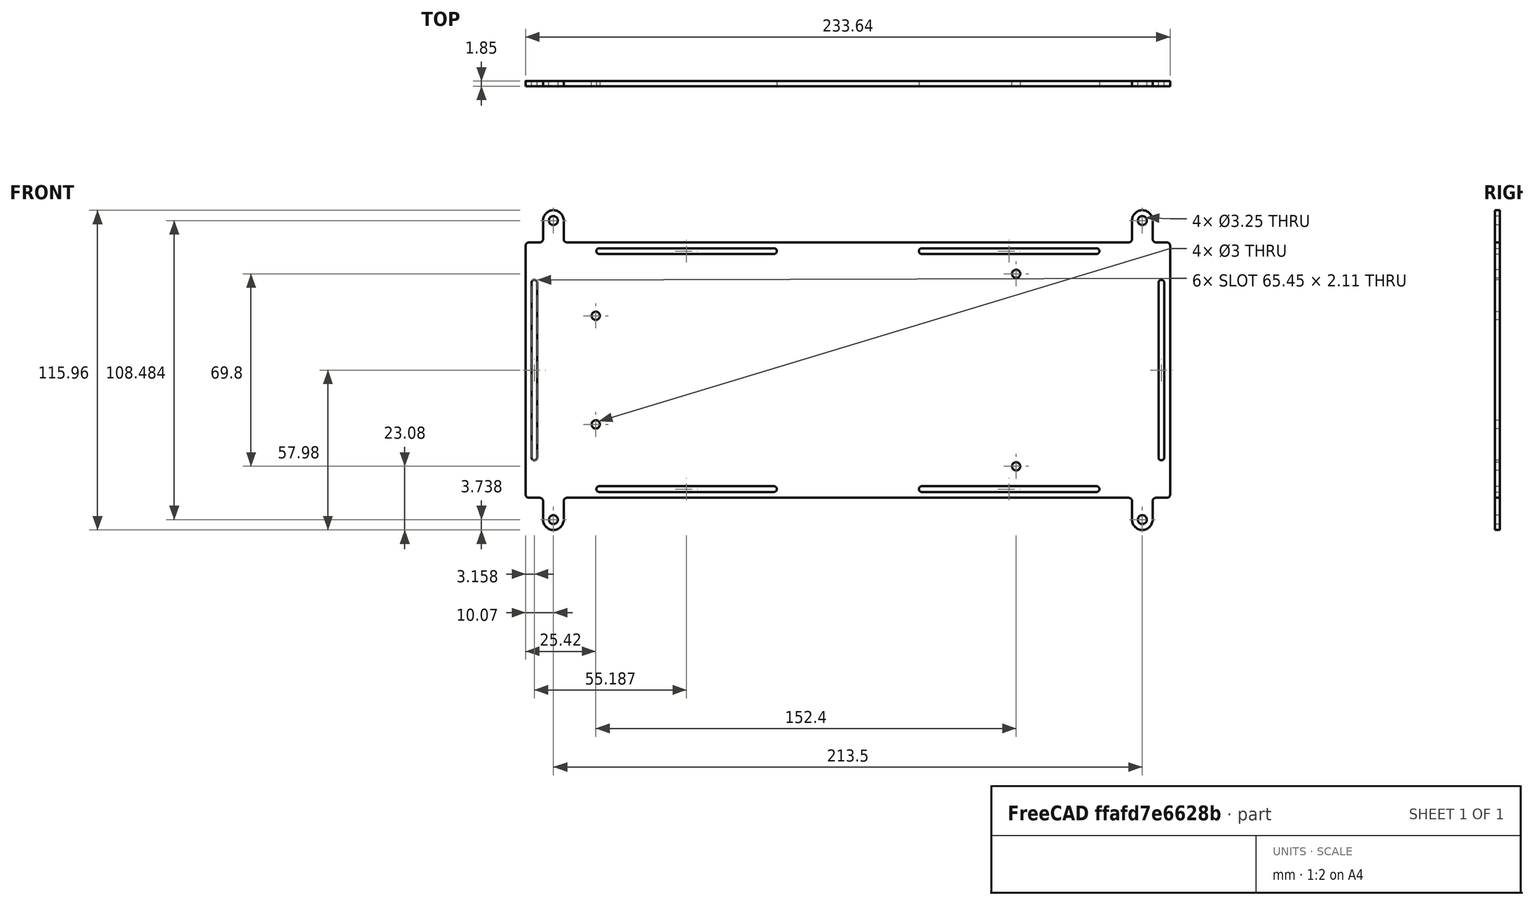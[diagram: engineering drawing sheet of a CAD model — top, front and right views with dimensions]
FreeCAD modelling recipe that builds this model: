
FCSTD DOCUMENT  (FreeCAD 1.0R38641 +468 (Git))
Label: psu_top_and_bottom
License: All rights reserved
LicenseURL: https://en.wikipedia.org/wiki/All_rights_reserved
objects: PartDesign::SubShapeBinder×2, Sketcher::SketchObject×1, PartDesign::Pad×1, PartDesign::Body×1
note: 8 computed .brp shape members not serialized (recipe doc carries the construction recipe); baked Part::Feature solids carry a one-line shape summary decoded from their .brp
EXTERNAL_REF file=../panel_back.FCStd obj=Body
EXTERNAL_REF file=../../third_party/doepfer_psu3.FCStd obj=Sketch
EXTERNAL_REF file=../panel_back.FCStd obj=Sketch
EXTERNAL_REF file=../../third_party/doepfer_psu3.FCStd obj=Body
EXTERNAL_REF file=../dimensions.FCStd obj=VarSet

FEATURE [PartDesign::SubShapeBinder] Binder  label="PanelBackBinder"
  BindCopyOnChange = 0
  BindMode = 0
  ClaimChildren = false
  Context = -> Body [Binder.]
  Fuse = false
  MakeFace = true
  OffsetFill = false
  OffsetIntersection = false
  OffsetJoinType = 0
  OffsetOpenResult = false
  PartialLoad = false
  Refine = true
  Relative = true
  Support = -> [<external ../panel_back.FCStd>#Body]
  _Version = 2
FEATURE [PartDesign::SubShapeBinder] Binder001  label="Psu3Binder"
  BindCopyOnChange = 0
  BindMode = 0
  ClaimChildren = false
  Context = -> Body [Binder001.]
  Fuse = false
  MakeFace = true
  OffsetFill = false
  OffsetIntersection = false
  OffsetJoinType = 0
  OffsetOpenResult = false
  PartialLoad = false
  Placement = pos=(103,130,-16.25) rot=(1,0,0;-1.5708rad)
  Refine = true
  Relative = true
  Support = -> [<external ../../third_party/doepfer_psu3.FCStd>#Body]
  _Version = 2
  expr: .Placement.Base.x = (panel_back#Sketch.Constraints.DeltaX - panel_back#Sketch.Constraints.OffsetX - doepfer_psu3#Sketch.Constraints.Width) / 2 - 10 mm
  expr: .Placement.Base.z = (doepfer_psu3#Sketch.Constraints.Height - (panel_back#Sketch.Constraints.DeltaY - panel_back#Sketch.Constraints.OffsetY)) / 2
FEATURE [Sketcher::SketchObject] Sketch
  ArcFitTolerance = 1e-06
  AttachmentSupport = -> [Binder]
  ExternalGeometry = -> [Binder001,Binder]
  FullyConstrained = true
  MakeInternals = false
  MapMode = 5
  Placement = pos=(0,127.227,-5.85e-14) rot=(0,0.707107,0.707107;3.14159rad)
  expr: Constraints[113] = dimensions#VarSet.EnclosureFinishThickness
  expr: Constraints[36] = dimensions#VarSet.EnclosureTotalThickness + 2 * dimensions#VarSet.EnclosureFinishThickness
  sketch-geometry (95):
    g0: LineSegment StartX=-330.325 StartY=-11.1254 StartZ=0 EndX=-330.325 EndY=-101.375 EndZ=0
    g1: LineSegment StartX=-96.6754 StartY=-101.375 StartZ=0 EndX=-96.6754 EndY=-11.1254 EndZ=0
    g2: Circle CenterX=-320.25 CenterY=-2.0081 CenterZ=0 NormalX=0 NormalY=0 NormalZ=1 AngleXU=0 Radius=1.627
    g3: Circle CenterX=-106.75 CenterY=-2.0081 CenterZ=0 NormalX=0 NormalY=0 NormalZ=1 AngleXU=0 Radius=1.627
    g4: Circle CenterX=-122.1 CenterY=-36.55 CenterZ=0 NormalX=0 NormalY=0 NormalZ=1 AngleXU=0 Radius=1.5
    g5: Circle CenterX=-122.1 CenterY=-75.95 CenterZ=0 NormalX=0 NormalY=0 NormalZ=1 AngleXU=0 Radius=1.5
    g6: Circle CenterX=-106.75 CenterY=-110.492 CenterZ=0 NormalX=0 NormalY=0 NormalZ=1 AngleXU=0 Radius=1.627
    g7: Circle CenterX=-320.25 CenterY=-110.492 CenterZ=0 NormalX=0 NormalY=0 NormalZ=1 AngleXU=0 Radius=1.627
    g8: Circle CenterX=-274.5 CenterY=-91.15 CenterZ=0 NormalX=0 NormalY=0 NormalZ=1 AngleXU=0 Radius=1.5
    g9: Circle CenterX=-274.5 CenterY=-21.35 CenterZ=0 NormalX=0 NormalY=0 NormalZ=1 AngleXU=0 Radius=1.5
    g10: ArcOfCircle CenterX=-329.125 CenterY=-11.1254 CenterZ=0 NormalX=0 NormalY=0 NormalZ=1 AngleXU=0 Radius=1.2 StartAngle=1.5708 EndAngle=3.14159
    g11: GeomPoint [constr] X=-330.325 Y=-9.9254 Z=0
    g12: ArcOfCircle CenterX=-329.125 CenterY=-101.375 CenterZ=0 NormalX=0 NormalY=0 NormalZ=1 AngleXU=0 Radius=1.2 StartAngle=3.14159 EndAngle=4.71239
    g13: GeomPoint [constr] X=-330.325 Y=-102.575 Z=0
    g14: ArcOfCircle CenterX=-97.8754 CenterY=-101.375 CenterZ=0 NormalX=0 NormalY=0 NormalZ=1 AngleXU=0 Radius=1.2 StartAngle=4.71239 EndAngle=6.28319
    g15: GeomPoint [constr] X=-96.6754 Y=-102.575 Z=0
    g16: ArcOfCircle CenterX=-97.8754 CenterY=-11.1254 CenterZ=0 NormalX=0 NormalY=0 NormalZ=1 AngleXU=0 Radius=1.2 StartAngle=2e-16 EndAngle=1.5708
    g17: GeomPoint [constr] X=-96.6754 Y=-9.9254 Z=0
    g18: ArcOfCircle CenterX=-327.162 CenterY=-24.579 CenterZ=0 NormalX=0 NormalY=0 NormalZ=1 AngleXU=0 Radius=1.0541 StartAngle=-9e-16 EndAngle=3.14159
    g19: ArcOfCircle CenterX=-327.162 CenterY=-87.921 CenterZ=0 NormalX=0 NormalY=0 NormalZ=1 AngleXU=0 Radius=1.0541 StartAngle=3.14159 EndAngle=6.28319
    g20: LineSegment StartX=-326.108 StartY=-24.579 StartZ=0 EndX=-326.108 EndY=-87.921 EndZ=0
    g21: LineSegment StartX=-328.216 StartY=-24.579 StartZ=0 EndX=-328.216 EndY=-87.921 EndZ=0
    g22: LineSegment [constr] StartX=-330.325 StartY=-56.25 StartZ=0 EndX=-328.216 EndY=-56.25 EndZ=0
    g23: ArcOfCircle CenterX=-99.8377 CenterY=-24.579 CenterZ=0 NormalX=0 NormalY=0 NormalZ=1 AngleXU=0 Radius=1.0541 StartAngle=-9e-16 EndAngle=3.14159
    g24: ArcOfCircle CenterX=-99.8377 CenterY=-87.921 CenterZ=0 NormalX=0 NormalY=0 NormalZ=1 AngleXU=0 Radius=1.0541 StartAngle=3.14159 EndAngle=6.28319
    g25: LineSegment StartX=-98.7836 StartY=-24.579 StartZ=0 EndX=-98.7836 EndY=-87.921 EndZ=0
    g26: LineSegment StartX=-100.892 StartY=-24.579 StartZ=0 EndX=-100.892 EndY=-87.921 EndZ=0
    g27: LineSegment [constr] StartX=-98.7836 StartY=-56.25 StartZ=0 EndX=-96.6754 EndY=-56.25 EndZ=0
    g28: ArcOfCircle CenterX=-303.647 CenterY=-13.0877 CenterZ=0 NormalX=0 NormalY=0 NormalZ=1 AngleXU=0 Radius=1.0541 StartAngle=1.5708 EndAngle=4.71239
    g29: ArcOfCircle CenterX=-240.305 CenterY=-13.0877 CenterZ=0 NormalX=0 NormalY=0 NormalZ=1 AngleXU=0 Radius=1.0541 StartAngle=4.71239 EndAngle=7.85398
    g30: LineSegment StartX=-303.647 StartY=-12.0336 StartZ=0 EndX=-240.305 EndY=-12.0336 EndZ=0
    g31: LineSegment StartX=-303.647 StartY=-14.1418 StartZ=0 EndX=-240.305 EndY=-14.1418 EndZ=0
    g32: ArcOfCircle CenterX=-186.695 CenterY=-13.0877 CenterZ=0 NormalX=0 NormalY=0 NormalZ=1 AngleXU=0 Radius=1.0541 StartAngle=1.5708 EndAngle=4.71239
    g33: ArcOfCircle CenterX=-123.353 CenterY=-13.0877 CenterZ=0 NormalX=0 NormalY=0 NormalZ=1 AngleXU=0 Radius=1.0541 StartAngle=4.71239 EndAngle=7.85398
    g34: LineSegment StartX=-186.695 StartY=-12.0336 StartZ=0 EndX=-123.353 EndY=-12.0336 EndZ=0
    g35: LineSegment StartX=-186.695 StartY=-14.1418 StartZ=0 EndX=-123.353 EndY=-14.1418 EndZ=0
    g36: ArcOfCircle CenterX=-303.647 CenterY=-99.4123 CenterZ=0 NormalX=0 NormalY=0 NormalZ=1 AngleXU=0 Radius=1.0541 StartAngle=1.5708 EndAngle=4.71239
    g37: ArcOfCircle CenterX=-240.305 CenterY=-99.4123 CenterZ=0 NormalX=0 NormalY=0 NormalZ=1 AngleXU=0 Radius=1.0541 StartAngle=4.71239 EndAngle=7.85398
    g38: LineSegment StartX=-303.647 StartY=-98.3582 StartZ=0 EndX=-240.305 EndY=-98.3582 EndZ=0
    g39: LineSegment StartX=-303.647 StartY=-100.466 StartZ=0 EndX=-240.305 EndY=-100.466 EndZ=0
    g40: ArcOfCircle CenterX=-186.695 CenterY=-99.4123 CenterZ=0 NormalX=0 NormalY=0 NormalZ=1 AngleXU=0 Radius=1.0541 StartAngle=1.5708 EndAngle=4.71239
    g41: ArcOfCircle CenterX=-123.353 CenterY=-99.4123 CenterZ=0 NormalX=0 NormalY=0 NormalZ=1 AngleXU=0 Radius=1.0541 StartAngle=4.71239 EndAngle=7.85398
    g42: LineSegment StartX=-186.695 StartY=-98.3582 StartZ=0 EndX=-123.353 EndY=-98.3582 EndZ=0
    g43: LineSegment StartX=-186.695 StartY=-100.466 StartZ=0 EndX=-123.353 EndY=-100.466 EndZ=0
    g44: LineSegment [constr] StartX=-271.976 StartY=-100.466 StartZ=0 EndX=-271.976 EndY=-102.575 EndZ=0
    g45: LineSegment [constr] StartX=-155.024 StartY=-100.466 StartZ=0 EndX=-155.024 EndY=-102.575 EndZ=0
    g46: LineSegment [constr] StartX=-155.024 StartY=-12.0336 StartZ=0 EndX=-155.024 EndY=-9.9254 EndZ=0
    g47: LineSegment [constr] StartX=-271.976 StartY=-12.0336 StartZ=0 EndX=-271.976 EndY=-9.9254 EndZ=0
    g48: LineSegment [constr] StartX=-271.976 StartY=-98.3582 StartZ=0 EndX=-271.976 EndY=-14.1418 EndZ=0
    g49: LineSegment [constr] StartX=-155.024 StartY=-14.1418 StartZ=0 EndX=-155.024 EndY=-98.3582 EndZ=0
    g50: LineSegment [constr] StartX=-257.002 StartY=2.8729 StartZ=0 EndX=-257.002 EndY=-9.9254 EndZ=0
    g51: LineSegment [constr] StartX=-257.002 StartY=-115.373 StartZ=0 EndX=-257.002 EndY=-102.575 EndZ=0
    g52: LineSegment [constr] StartX=-328.216 StartY=-56.25 StartZ=0 EndX=-326.108 EndY=-56.25 EndZ=0
    g53: LineSegment [constr] StartX=-213.5 StartY=-9.9254 StartZ=0 EndX=-213.5 EndY=-102.575 EndZ=0
    g54: LineSegment [constr] StartX=-213.627 StartY=-9.9254 StartZ=0 EndX=-213.627 EndY=-102.575 EndZ=0
    g55: LineSegment [constr] StartX=-330.325 StartY=-98.3582 StartZ=0 EndX=-271.976 EndY=-98.3582 EndZ=0
    g56: LineSegment [constr] StartX=-271.976 StartY=-98.3582 StartZ=0 EndX=-213.627 EndY=-98.3582 EndZ=0
    g57: LineSegment [constr] StartX=-155.024 StartY=-98.3582 StartZ=0 EndX=-96.6754 EndY=-98.3582 EndZ=0
    g58: LineSegment [constr] StartX=-240.305 StartY=-14.1418 StartZ=0 EndX=-240.305 EndY=-16.25 EndZ=0
    g59: LineSegment [constr] StartX=-103 StartY=-56.25 StartZ=0 EndX=-100.892 EndY=-56.25 EndZ=0
    g60: ArcOfCircle CenterX=-320.25 CenterY=-2.0081 CenterZ=0 NormalX=0 NormalY=0 NormalZ=1 AngleXU=0 Radius=3.7352 StartAngle=0 EndAngle=3.14159
    g61: LineSegment StartX=-316.515 StartY=-2.0081 StartZ=0 EndX=-316.515 EndY=-8.7254 EndZ=0
    g62: LineSegment StartX=-325.185 StartY=-9.9254 StartZ=0 EndX=-329.125 EndY=-9.9254 EndZ=0
    g63: LineSegment StartX=-329.125 StartY=-102.575 StartZ=0 EndX=-325.185 EndY=-102.575 EndZ=0
    g64: LineSegment StartX=-315.315 StartY=-102.575 StartZ=0 EndX=-111.685 EndY=-102.575 EndZ=0
    g65: LineSegment StartX=-101.815 StartY=-102.575 StartZ=0 EndX=-97.8754 EndY=-102.575 EndZ=0
    g66: LineSegment StartX=-111.685 StartY=-9.9254 StartZ=0 EndX=-315.315 EndY=-9.9254 EndZ=0
    g67: LineSegment StartX=-97.8754 StartY=-9.9254 StartZ=0 EndX=-101.815 EndY=-9.9254 EndZ=0
    g68: ArcOfCircle CenterX=-320.25 CenterY=-110.492 CenterZ=0 NormalX=0 NormalY=0 NormalZ=1 AngleXU=0 Radius=3.7352 StartAngle=3.14159 EndAngle=6.28319
    g69: ArcOfCircle CenterX=-106.75 CenterY=-110.492 CenterZ=0 NormalX=0 NormalY=0 NormalZ=1 AngleXU=0 Radius=3.7352 StartAngle=3.14159 EndAngle=6.28319
    g70: ArcOfCircle CenterX=-106.75 CenterY=-2.0081 CenterZ=0 NormalX=0 NormalY=0 NormalZ=1 AngleXU=0 Radius=3.7352 StartAngle=0 EndAngle=3.14159
    g71: LineSegment StartX=-323.985 StartY=-2.0081 StartZ=0 EndX=-323.985 EndY=-8.7254 EndZ=0
    g72: LineSegment StartX=-323.985 StartY=-110.492 StartZ=0 EndX=-323.985 EndY=-103.775 EndZ=0
    g73: LineSegment StartX=-316.515 StartY=-110.492 StartZ=0 EndX=-316.515 EndY=-103.775 EndZ=0
    g74: LineSegment StartX=-110.485 StartY=-110.492 StartZ=0 EndX=-110.485 EndY=-103.775 EndZ=0
    g75: LineSegment StartX=-103.015 StartY=-110.492 StartZ=0 EndX=-103.015 EndY=-103.775 EndZ=0
    g76: LineSegment StartX=-110.485 StartY=-2.0081 StartZ=0 EndX=-110.485 EndY=-8.7254 EndZ=0
    g77: LineSegment StartX=-103.015 StartY=-2.0081 StartZ=0 EndX=-103.015 EndY=-8.7254 EndZ=0
    g78: LineSegment [constr] StartX=-318.623 StartY=-110.492 StartZ=0 EndX=-316.515 EndY=-110.492 EndZ=0
    g79: ArcOfCircle CenterX=-325.185 CenterY=-8.7254 CenterZ=0 NormalX=0 NormalY=0 NormalZ=1 AngleXU=0 Radius=1.2 StartAngle=4.71239 EndAngle=6.28319
    g80: GeomPoint [constr] X=-323.985 Y=-9.9254 Z=0
    g81: ArcOfCircle CenterX=-315.315 CenterY=-8.7254 CenterZ=0 NormalX=0 NormalY=0 NormalZ=1 AngleXU=0 Radius=1.2 StartAngle=3.14159 EndAngle=4.71239
    g82: GeomPoint [constr] X=-316.515 Y=-9.9254 Z=0
    g83: ArcOfCircle CenterX=-111.685 CenterY=-8.7254 CenterZ=0 NormalX=0 NormalY=0 NormalZ=1 AngleXU=0 Radius=1.2 StartAngle=4.71239 EndAngle=6.28319
    g84: GeomPoint [constr] X=-110.485 Y=-9.9254 Z=0
    g85: ArcOfCircle CenterX=-101.815 CenterY=-8.7254 CenterZ=0 NormalX=0 NormalY=0 NormalZ=1 AngleXU=0 Radius=1.2 StartAngle=3.14159 EndAngle=4.71239
    g86: GeomPoint [constr] X=-103.015 Y=-9.9254 Z=0
    g87: ArcOfCircle CenterX=-111.685 CenterY=-103.775 CenterZ=0 NormalX=0 NormalY=0 NormalZ=1 AngleXU=0 Radius=1.2 StartAngle=4.8e-15 EndAngle=1.5708
    g88: GeomPoint [constr] X=-110.485 Y=-102.575 Z=0
    g89: ArcOfCircle CenterX=-101.815 CenterY=-103.775 CenterZ=0 NormalX=0 NormalY=0 NormalZ=1 AngleXU=0 Radius=1.2 StartAngle=1.5708 EndAngle=3.14159
    g90: GeomPoint [constr] X=-103.015 Y=-102.575 Z=0
    g91: ArcOfCircle CenterX=-325.185 CenterY=-103.775 CenterZ=0 NormalX=0 NormalY=0 NormalZ=1 AngleXU=0 Radius=1.2 StartAngle=3.3e-15 EndAngle=1.5708
    g92: GeomPoint [constr] X=-323.985 Y=-102.575 Z=0
    g93: ArcOfCircle CenterX=-315.315 CenterY=-103.775 CenterZ=0 NormalX=0 NormalY=0 NormalZ=1 AngleXU=0 Radius=1.2 StartAngle=1.5708 EndAngle=3.14159
    g94: GeomPoint [constr] X=-316.515 Y=-102.575 Z=0
  constraints (223):
    c: Vertical(g1)
    c: Coincident(g2,g-7)
    c: Equal(g2,g-7)
    c: Coincident(g3,g-10)
    c: Equal(g3,g-10)
    c: Coincident(g4,g-4)
    c: Equal(g4,g-4)
    c: Coincident(g5,g-5)
    c: Equal(g5,g-5)
    c: Coincident(g6,g-9)
    c: Equal(g6,g-9)
    c: Coincident(g7,g-8)
    c: Equal(g7,g-8)
    c: Coincident(g8,g-6)
    c: Equal(g8,g-6)
    c: Coincident(g9,g-3)
    c: Equal(g9,g-3)
    c: PointOnObject(g11,g0)
    c: Tangent(g0,g10) = -1.5708
    c: PointOnObject(g13,g0)
    c: Tangent(g0,g12) = -1.5708
    c: PointOnObject(g15,g1)
    c: Tangent(g1,g14) = -1.5708
    c: PointOnObject(g17,g1)
    c: Tangent(g1,g16) = -1.5708
    c: Equal(g-11,g10)
    c: Equal(g10,g12)
    c: Equal(g12,g14)
    c: Equal(g14,g16)
    c: Tangent(g18,g20) = 1.5708
    c: Tangent(g18,g21) = -1.5708
    c: Tangent(g19,g20) = 1.5708
    c: Tangent(g19,g21) = -1.5708
    c: Equal(g18,g19)
    c: Vertical(g20)
    c: Equal(g21,g-14)
    c: Distance(g20,g21) = 2.1082
    c: Symmetric(g0,g0,g22)
    c: Symmetric(g21,g21,g22)
    c: Horizontal(g22)
    c: Tangent(g23,g25) = 1.5708
    c: Tangent(g23,g26) = -1.5708
    c: Tangent(g24,g25) = 1.5708
    c: Tangent(g24,g26) = -1.5708
    c: Equal(g23,g24)
    c: Vertical(g26)
    c: Equal(g26,g21)
    c: Equal(g23,g18)
    c: Symmetric(g25,g25,g27)
    c: Symmetric(g1,g1,g27)
    c: Horizontal(g27)
    c: Equal(g27,g22)
    c: Tangent(g28,g30) = 1.5708
    c: Tangent(g28,g31) = -1.5708
    c: Tangent(g29,g30) = 1.5708
    c: Tangent(g29,g31) = -1.5708
    c: Equal(g28,g29)
    c: Horizontal(g30)
    c: Tangent(g32,g34) = 1.5708
    c: Tangent(g32,g35) = -1.5708
    c: Tangent(g33,g34) = 1.5708
    c: Tangent(g33,g35) = -1.5708
    c: Equal(g32,g33)
    c: Horizontal(g34)
    c: Equal(g29,g32)
    c: Equal(g18,g28)
    c: Tangent(g36,g38) = 1.5708
    c: Tangent(g36,g39) = -1.5708
    c: Tangent(g37,g38) = 1.5708
    c: Tangent(g37,g39) = -1.5708
    c: Equal(g36,g37)
    c: Horizontal(g38)
    c: Tangent(g40,g42) = 1.5708
    c: Tangent(g40,g43) = -1.5708
    c: Tangent(g41,g42) = 1.5708
    c: Tangent(g41,g43) = -1.5708
    c: Equal(g40,g41)
    c: Horizontal(g42)
    c: Equal(g41,g24)
    c: Equal(g40,g37)
    c: Symmetric(g39,g39,g44)
    c: Vertical(g44)
    c: Symmetric(g43,g43,g45)
    c: Vertical(g45)
    c: Symmetric(g34,g34,g46)
    c: Vertical(g46)
    c: Symmetric(g30,g30,g47)
    c: Vertical(g47)
    c: Symmetric(g38,g38,g48)
    c: Symmetric(g31,g31,g48)
    c: Vertical(g48)
    c: Equal(g44,g22)
    c: Equal(g22,g47)
    c: Equal(g47,g46)
    c: Equal(g45,g46)
    c: Symmetric(g35,g35,g49)
    c: Symmetric(g42,g42,g49)
    c: Vertical(g49)
    c: Equal(g42,g38)
    c: Equal(g38,g31)
    c: Equal(g35,g42)
    c: Equal(g31,g20)
    c: Symmetric(g-15,g-15,g50)
    c: Vertical(g50)
    c: PointOnObject(g51,g-12)
    c: Equal(g51,g50)
    c: Tangent(g51,g50)
    c: Coincident(g52,g22)
    c: Symmetric(g20,g20,g52)
    c: Equal(g52,g22)
    c: Symmetric(g67,g62,g53)
    c: Symmetric(g63,g65,g53)
    c: Vertical(g54)
    c: Distance(g53,g54) = 0.127
    c: PointOnObject(g55,g0)
    c: Horizontal(g55)
    c: Coincident(g56,g55)
    c: PointOnObject(g56,g54)
    c: Horizontal(g56)
    c: Equal(g55,g56)
    c: PointOnObject(g57,g1)
    c: Horizontal(g57)
    c: Equal(g57,g55)
    c: Coincident(g55,g48)
    c: Coincident(g57,g49)
    c: Coincident(g58,g29)
    c: PointOnObject(g58,g-16)
    c: Vertical(g58)
    c: Equal(g47,g58)
    c: Symmetric(g-17,g-17,g59)
    c: Symmetric(g26,g26,g59)
    c: Equal(g59,g27)
    c: Vertical(g0)
    c: Coincident(g60,g2)
    c: Vertical(g61)
    c: Horizontal(g62)
    c: Horizontal(g63)
    c: PointOnObject(g13,g63)
    c: PointOnObject(g15,g63)
    c: PointOnObject(g44,g63)
    c: PointOnObject(g45,g63)
    c: PointOnObject(g51,g63)
    c: PointOnObject(g54,g63)
    c: PointOnObject(g11,g67)
    c: PointOnObject(g17,g67)
    c: PointOnObject(g46,g67)
    c: PointOnObject(g47,g67)
    c: PointOnObject(g50,g67)
    c: PointOnObject(g54,g67)
    c: Coincident(g68,g7)
    c: Coincident(g69,g6)
    c: Coincident(g70,g3)
    c: Vertical(g71)
    c: Vertical(g72)
    c: Vertical(g73)
    c: Vertical(g74)
    c: Vertical(g75)
    c: Vertical(g76)
    c: Vertical(g77)
    c: Tangent(g76,g70) = -1.5708
    c: Tangent(g77,g70) = 1.5708
    c: Tangent(g61,g60) = 1.5708
    c: Tangent(g71,g60) = -1.5708
    c: Tangent(g68,g73) = -1.5708
    c: Tangent(g72,g68) = 1.5708
    c: Tangent(g69,g74) = 1.5708
    c: Tangent(g69,g75) = -1.5708
    c: Tangent(g65,g64)
    c: Tangent(g64,g63)
    c: Tangent(g62,g66)
    c: Tangent(g67,g66)
    c: Equal(g68,g60)
    c: Equal(g60,g70)
    c: Equal(g70,g69)
    c: Tangent(g12,g63) = -1.5708
    c: Tangent(g10,g62) = -1.5708
    c: Tangent(g16,g67) = -1.5708
    c: Tangent(g14,g65) = -1.5708
    c: PointOnObject(g78,g7)
    c: Coincident(g78,g68)
    c: Horizontal(g78)
    c: Equal(g78,g44)
    c: PointOnObject(g80,g62)
    c: PointOnObject(g80,g71)
    c: Tangent(g62,g79) = 1.5708
    c: Tangent(g71,g79) = 1.5708
    c: PointOnObject(g82,g61)
    c: PointOnObject(g82,g66)
    c: Tangent(g61,g81) = -1.5708
    c: Tangent(g66,g81) = 1.5708
    c: Equal(g79,g10)
    c: Equal(g79,g81)
    c: PointOnObject(g84,g66)
    c: PointOnObject(g84,g76)
    c: Tangent(g66,g83) = 1.5708
    c: Tangent(g76,g83) = 1.5708
    c: PointOnObject(g86,g67)
    c: PointOnObject(g86,g77)
    c: Tangent(g67,g85) = 1.5708
    c: Tangent(g77,g85) = -1.5708
    c: Equal(g83,g85)
    c: Equal(g85,g16)
    c: PointOnObject(g88,g64)
    c: PointOnObject(g88,g74)
    c: Tangent(g64,g87) = 1.5708
    c: Tangent(g74,g87) = -1.5708
    c: PointOnObject(g90,g65)
    c: PointOnObject(g90,g75)
    c: Tangent(g65,g89) = 1.5708
    c: Tangent(g75,g89) = 1.5708
    c: Equal(g89,g14)
    c: Equal(g87,g89)
    c: PointOnObject(g92,g63)
    c: PointOnObject(g92,g72)
    c: Tangent(g63,g91) = 1.5708
    c: Tangent(g72,g91) = -1.5708
    c: PointOnObject(g94,g64)
    c: PointOnObject(g94,g73)
    c: Tangent(g64,g93) = 1.5708
    c: Tangent(g73,g93) = 1.5708
    c: Equal(g93,g91)
    c: Equal(g91,g12)
    c: Equal(g63,g65)
FEATURE [PartDesign::Pad] Pad
  Direction = (0,1,-2e-16)
  Length = 1.8542
  Length2 = 10
  Profile = -> Sketch
  ReferenceAxis = -> Sketch [N_Axis]
  Refine = true
  Suppressed = false
  Type = 0
  expr: Length = dimensions#VarSet.EnclosureTotalThickness
FEATURE [PartDesign::Body] Body  label="PsuTopAndBottom"
  AllowCompound = false
  Group = -> [Binder,Binder001,Sketch,Pad]
  Origin = -> Origin
  Tip = -> Pad
